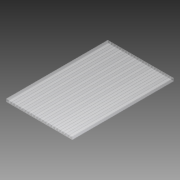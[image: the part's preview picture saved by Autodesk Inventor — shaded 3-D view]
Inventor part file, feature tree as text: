
AUTODESK INVENTOR PART (.ipt)
format: ipt  version: 2012 (Build 160160000, 160)  size: 179,712 bytes
history: native  units: in
note: dims shown in document units (in); Inventor stores cm internally (conversion verified against a paired STEP export)
features: extrude x1, sketch x1
ambient origin geometry x8: Origin, YZ Plane, XZ Plane, XY Plane, X Axis, Y Axis, Z Axis, Center Point
bodies: Solid1 (feature_tree)
feature tree (2):
  extrude  "Extrusion1"  Depth=0.25in
  sketch  "Sketch1"  dims[d0=5.77in d1=0.25in d2=0.0201in d3=0.02in d4=0.02in d5=0.23in d6=9.0551in d8=0.25in d9=0.3937in d11=1.0in d13=8.875in d14=0.0in]
